# Revit family: Building-IEC309Connections-GEWISS-67IB-INTERLOCKED-SOCKET-OUTLETS_IP67_WITH_BOTTOM_63A_FUS
name_source: partatom
category: Apparecchi elettrici
units: mm (PartAtom-declared; Revit-internal decimal feet)

## family parameters
Condiviso = Sì
Host = Superficie
Mantenere orientamento annotazione = Sì
Punto di calcolo locali = Sì
Quota connettore circolare = Usa diametro
Taglio con vuoti quando caricato = Sì
Tipo di parte = Normale

## types (11) — shared parameters
Catalogue = BUILDING
Catalogue Range = 67 IB
Corpo presa = GEWISS -BLU
Electrocod = 2222
Frequency = 50/60 Hz
Fuse breacking capacity = > 50 kA
Glow Wire Test = 850 °C (IB socket) - 650 °C (bottom)
Glow wire test: = 850 °C (IB socket) - 650 °C (bottom)
IDF = 1711c5f6-abc8-487c-ac1f-1400d1f361c6
IDT = c3a9b50e-4e9d-4f00-afb7-28748640f89d
IP degree = IP67
Immagine tipo = L.jpg
Operating temperature: = -25 +40 °C
Potenza in wolt = 0 V
Produttore = GEWISS S.p.A.
Prospetto di default = 1219 mm
Protection = Fuse-holder base (CBF)
Rated current (A) = 63
Rated current (In) = 63
Rated frequency (Hz) = 50/60 Hz
Rated impulse withstand voltage = 4KV
Rated insulation voltage (Ui) = 500V
Rated short-circuit current (Icc) = 10KA
SEO = Socket outlet
Shock resistance = IK08
Simbolo presa = PRESAINDSTAGNA : 3P
Struttura = Grigio RAL - 7035
Technical sheet = https://www.gewiss.com
Thermo-pressure with ball = 125 °C (IB socket) - 80 °C (bottom)
Type of fuse = Ã˜ 22x58 mm
Typology = Vertical
URL = https://www.gewiss.com
Version file RFA = 21.4
Weight = Max. 2.5 Kg
Weight (kg) = Max. 2.5 Kg
With back-mounting box = Yes
Working temperature = -25 ÷ +40 °C
npoli = 1
presa = rosso
zero-valued in all types: giallo

## per-type parameters (varying)
| type | Colour | Colour: | Descrizione | EAN code | IB socket outlet rated current (In) | Modello | No. of poles | Number of poles | Rated voltage | Rated voltage: | Reference h |
| GW67254N - 3P+E 63A 500V V.INT.SOCK.O.W.B.7H CBF | Black | Black | 3P+E 63A 500V V.INT.SOCK.O.W.B.7H CBF | 8011564742246 | 52A | GW67254N | 3P+E | 3P+E | 480 - 500 V | 480 - 500 V | 7 |
| GW67248N - 2P+E 63A 230V V.INT.SOCK.O.W.B.6H CBF | Blue | Blue | 2P+E 63A 230V V.INT.SOCK.O.W.B.6H CBF | 8011564742185 | 54A | GW67248N | 2P+E | 2P+E | 200 - 250 V | 200 - 250 V | 6 |
| GW67253N - 3P+N+T 63A 400V V.INT.SOCK.O.W.B.6H CBF | Red | Red | 3P+N+T 63A 400V V.INT.SOCK.O.W.B.6H CBF | 8011564742239 | 48A | GW67253N | 3P+N+E | 3P+N+E | 380 - 415 V | 380 - 415 V | 6 |
| GW67247N - 3P+N+T 63A 110V V.INT.SOCK.O.W.B.4H CBF | Yellow | Yellow | 3P+N+T 63A 110V V.INT.SOCK.O.W.B.4H CBF | 8011564742178 | 48A | GW67247N | 3P+N+E | 3P+N+E | 100 - 130 V | 100 - 130 V | 4 |
| GW67252N - 3P+E 63A 400V V.INT.SOCK.O.W.B.6H CBF | Red | Red | 3P+E 63A 400V V.INT.SOCK.O.W.B.6H CBF | 8011564742222 | 52A | GW67252N | 3P+E | 3P+E | 380 - 415 V | 380 - 415 V | 6 |
| GW67255N - 3P+N+T 63A 500V V.INT.SOCK.O.W.B.7H CBF | Black | Black | 3P+N+T 63A 500V V.INT.SOCK.O.W.B.7H CBF | 8011564742253 | 48A | GW67255N | 3P+N+E | 3P+N+E | 480 - 500 V | 480 - 500 V | 7 |
| GW67245N - 2P+E 63A 110V V.INT.SOCK.O.W.B.4H CBF | Yellow | Yellow | 2P+E 63A 110V V.INT.SOCK.O.W.B.4H CBF | 8011564742154 | 54A | GW67245N | 2P+E | 2P+E | 100 - 130 V | 100 - 130 V | 4 |
| GW67251N - 2P+E 63A 400V V.INT.SOCK.O.W.B.9H CBF | Red | Red | 2P+E 63A 400V V.INT.SOCK.O.W.B.9H CBF | 8011564742215 | 54A | GW67251N | 2P+E | 2P+E | 380 - 415 V | 380 - 415 V | 9 |
| GW67246N - 3P+E 63A 110V V.INT.SOCK.O.W.B.4H CBF | Yellow | Yellow | 3P+E 63A 110V V.INT.SOCK.O.W.B.4H CBF | 8011564742161 | 52A | GW67246N | 3P+E | 3P+E | 100 - 130 V | 100 - 130 V | 4 |
| GW67250N - 3P+N+T 63A 230V V.INT.SOCK.O.W.B.9H CBF | Blue | Blue | 3P+N+T 63A 230V V.INT.SOCK.O.W.B.9H CBF | 8011564742208 | 48A | GW67250N | 3P+N+E | 3P+N+E | 200 - 250 V | 200 - 250 V | 9 |
| GW67249N - 3P+E 63A 230V V.INT.SOCK.O.W.B.9H CBF | Blue | Blue | 3P+E 63A 230V V.INT.SOCK.O.W.B.9H CBF | 8011564742192 | 52A | GW67249N | 3P+E | 3P+E | 200 - 250 V | 200 - 250 V | 9 |

## geometry (parser evidence)
native form markers: Sweep x2
no freeform markers — native parametric forms only
